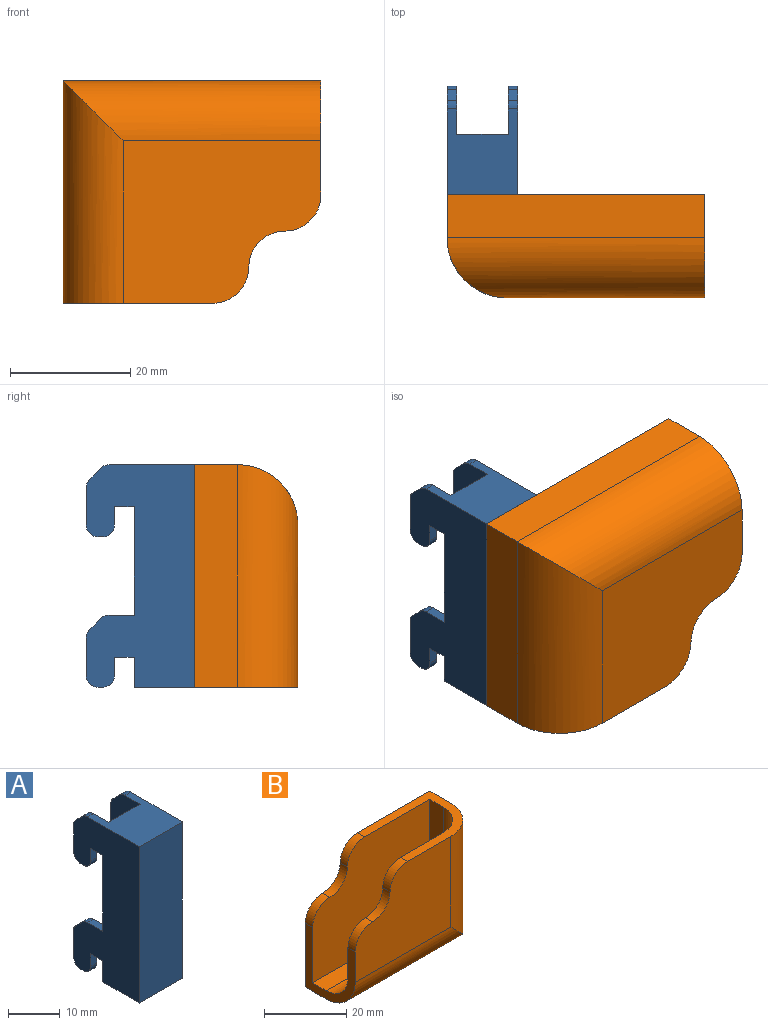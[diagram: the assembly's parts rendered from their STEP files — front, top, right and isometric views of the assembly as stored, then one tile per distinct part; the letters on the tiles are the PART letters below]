
ASSEMBLY  parts=2 mates=1
PART A: 48 faces, bbox 11.8x18x37 mm
  f0: plane 37x11.8mm, normal (0,1,0), area 391.8mm2, adj f1,f3,f4,f5,f6,f11,f12,f17
  f1: plane 14.17x11.8mm, normal (0,0,1), area 131.3mm2, adj f0,f2,f4,f5,f11,f31,f32,f44
  f2: plane 37x11.8mm, normal (0,-1,0), area 436.6mm2, adj f1,f3,f4,f5
  f3: plane 11.8x10mm, normal (0,0,-1), area 118mm2, adj f0,f2,f4,f5
  f4: plane 37x18mm, normal (-1,0,0), area 516.2mm2, adj f0,f1,f2,f3,f19,f20,f21,f22
  f5: plane 37x18mm, normal (1,0,0), area 516.2mm2, adj f0,f1,f2,f3,f6,f7,f8,f9
  f6: plane 3.3x1.6mm, normal (0,0,-1), area 5.3mm2, adj f0,f5,f7,f11
  f7: plane 3x1.6mm, normal (0,-1,0), area 4.8mm2, adj f5,f6,f11,f47
  f8: plane 1.6x0.7mm, normal (0,0,-1), area 1.1mm2, adj f5,f11,f46,f47
  f9: plane 6.17x1.6mm, normal (0,1,0), area 9.9mm2, adj f5,f11,f45,f46
  f10: plane 1.83x1.83mm, normal (0,0.71,0.71), area 4.1mm2, adj f5,f11,f44,f45
  f11: plane 12x8mm, normal (-1,0,0), area 73.1mm2, adj f0,f1,f6,f7,f8,f9,f10,f44
  f12: plane 3.3x1.6mm, normal (0,0,-1), area 5.3mm2, adj f0,f5,f13,f18
  f13: plane 3x1.6mm, normal (0,-1,0), area 4.8mm2, adj f5,f12,f18,f40
  f14: plane 1.6x0.7mm, normal (0,0,-1), area 1.1mm2, adj f5,f18,f40,f41
  f15: plane 6.17x1.6mm, normal (0,1,0), area 9.9mm2, adj f5,f18,f41,f42
  f16: plane 1.83x1.83mm, normal (0,0.71,0.71), area 4.1mm2, adj f5,f18,f42,f43
  f17: plane 4.17x1.6mm, normal (0,0,1), area 6.7mm2, adj f0,f5,f18,f43
  f18: plane 12x8mm, normal (-1,0,0), area 73.1mm2, adj f0,f12,f13,f14,f15,f16,f17,f40
  f19: plane 1.83x1.83mm, normal (0,0.71,0.71), area 4.1mm2, adj f4,f23,f38,f39
  f20: plane 6.17x1.6mm, normal (0,1,0), area 9.9mm2, adj f4,f23,f37,f38
  f21: plane 1.6x0.7mm, normal (0,0,-1), area 1.1mm2, adj f4,f23,f36,f37
  f22: plane 3x1.6mm, normal (0,-1,0), area 4.8mm2, adj f4,f23,f24,f36
  f23: plane 12x8mm, normal (1,0,0), area 73.1mm2, adj f0,f19,f20,f21,f22,f24,f25,f36
  f24: plane 3.3x1.6mm, normal (0,0,-1), area 5.3mm2, adj f0,f4,f22,f23
  f25: plane 4.17x1.6mm, normal (0,0,1), area 6.7mm2, adj f0,f4,f23,f39
  f26: plane 3.3x1.6mm, normal (0,0,-1), area 5.3mm2, adj f0,f4,f27,f31
  f27: plane 3x1.6mm, normal (0,-1,0), area 4.8mm2, adj f4,f26,f31,f35
  f28: plane 1.6x0.7mm, normal (0,0,-1), area 1.1mm2, adj f4,f31,f34,f35
  f29: plane 6.17x1.6mm, normal (0,1,0), area 9.9mm2, adj f4,f31,f33,f34
  f30: plane 1.83x1.83mm, normal (0,0.71,0.71), area 4.1mm2, adj f4,f31,f32,f33
  f31: plane 12x8mm, normal (1,0,0), area 73.1mm2, adj f0,f1,f26,f27,f28,f29,f30,f32
  f32: cylinder r=2mm len=1.6mm, axis (1,0,0), area 2.5mm2, adj f1,f4,f30,f31
  f33: cylinder r=2mm len=1.6mm, axis (-1,0,0), area 2.5mm2, adj f4,f29,f30,f31
  f34: cylinder r=2mm len=2mm, axis (-1,0,0), area 5mm2, adj f4,f28,f29,f31
  f35: cylinder r=2mm len=2mm, axis (-1,0,0), area 5mm2, adj f4,f27,f28,f31
  f36: cylinder r=2mm len=2mm, axis (-1,0,0), area 5mm2, adj f4,f21,f22,f23
  f37: cylinder r=2mm len=2mm, axis (-1,0,0), area 5mm2, adj f4,f20,f21,f23
  f38: cylinder r=2mm len=1.6mm, axis (-1,0,0), area 2.5mm2, adj f4,f19,f20,f23
  f39: cylinder r=2mm len=1.6mm, axis (-1,0,0), area 2.5mm2, adj f4,f19,f23,f25
  f40: cylinder r=2mm len=2mm, axis (1,0,0), area 5mm2, adj f5,f13,f14,f18
  f41: cylinder r=2mm len=2mm, axis (1,0,0), area 5mm2, adj f5,f14,f15,f18
  f42: cylinder r=2mm len=1.6mm, axis (1,0,0), area 2.5mm2, adj f5,f15,f16,f18
  f43: cylinder r=2mm len=1.6mm, axis (1,0,0), area 2.5mm2, adj f5,f16,f17,f18
  f44: cylinder r=2mm len=1.6mm, axis (-1,0,0), area 2.5mm2, adj f1,f5,f10,f11
  f45: cylinder r=2mm len=1.6mm, axis (1,0,0), area 2.5mm2, adj f5,f9,f10,f11
  f46: cylinder r=2mm len=2mm, axis (1,0,0), area 5mm2, adj f5,f8,f9,f11
  f47: cylinder r=2mm len=2mm, axis (1,0,0), area 5mm2, adj f5,f7,f8,f11
PART B: 20 faces, bbox 42.9x17.2x37 mm
  f0: plane 42.9x7.2mm, normal (0,0,-1), area 308.9mm2, adj f1,f3,f5,f7
  f1: plane 37x7.2mm, normal (1,0,0), area 266.4mm2, adj f0,f2,f5,f6
  f2: plane 24.9x17.2mm, normal (0,0,1), area 145.6mm2, adj f1,f4,f5,f6,f9,f10,f11,f12
  f3: plane 19x17.2mm, normal (-1,0,0), area 116.1mm2, adj f0,f4,f5,f7,f8,f10,f11,f13
  f4: plane 32.9x27mm, normal (0,-1,0), area 736.6mm2, adj f2,f3,f6,f7,f17,f18,f19
  f5: plane 42.9x37mm, normal (0,1,0), area 1435.6mm2, adj f0,f1,f2,f3,f14,f15,f16
  f6: cylinder r=10mm len=37mm, axis (0,0,-1), area 524.1mm2, adj f1,f2,f4,f7
  f7: cylinder r=10mm len=42.9mm, axis (-1,0,0), area 616.8mm2, adj f0,f3,f4,f6
  f8: plane 40.4x4.7mm, normal (0,0,1), area 189.9mm2, adj f3,f9,f11,f13
  f9: plane 34.5x4.7mm, normal (-1,0,0), area 162.1mm2, adj f2,f8,f11,f12
  f10: plane 32.9x27mm, normal (0,1,0), area 736.6mm2, adj f2,f3,f12,f13,f17,f18,f19
  f11: plane 40.4x34.5mm, normal (0,-1,0), area 1242.1mm2, adj f2,f3,f8,f9,f14,f15,f16
  f12: cylinder r=7.5mm len=34.5mm, axis (0,0,-1), area 374.3mm2, adj f2,f9,f10,f13
  f13: cylinder r=7.5mm len=40.4mm, axis (-1,0,0), area 443.8mm2, adj f3,f8,f10,f12
  f14: cylinder r=6mm len=6mm, axis (0,1,0), area 23.6mm2, adj f2,f5,f11,f15
  f15: cylinder r=6mm len=6mm, axis (0,1,0), area 23.6mm2, adj f5,f11,f14,f16
  f16: cylinder r=6mm len=6mm, axis (0,1,0), area 23.6mm2, adj f3,f5,f11,f15
  f17: cylinder r=6mm len=6mm, axis (0,1,0), area 23.6mm2, adj f3,f4,f10,f18
  f18: cylinder r=6mm len=6mm, axis (0,1,0), area 23.6mm2, adj f4,f10,f17,f19
  f19: cylinder r=6mm len=6mm, axis (0,1,0), area 23.6mm2, adj f2,f4,f10,f18
PLACE A t=(-0.7,0,0)mm
PLACE B rot(axis=(0,1,0),180deg) t=(-12.5,0,37)mm
MATE fastened B.f5 <-> A.f2  axis (0,1,0) through (-12.5,-10,37)mm
